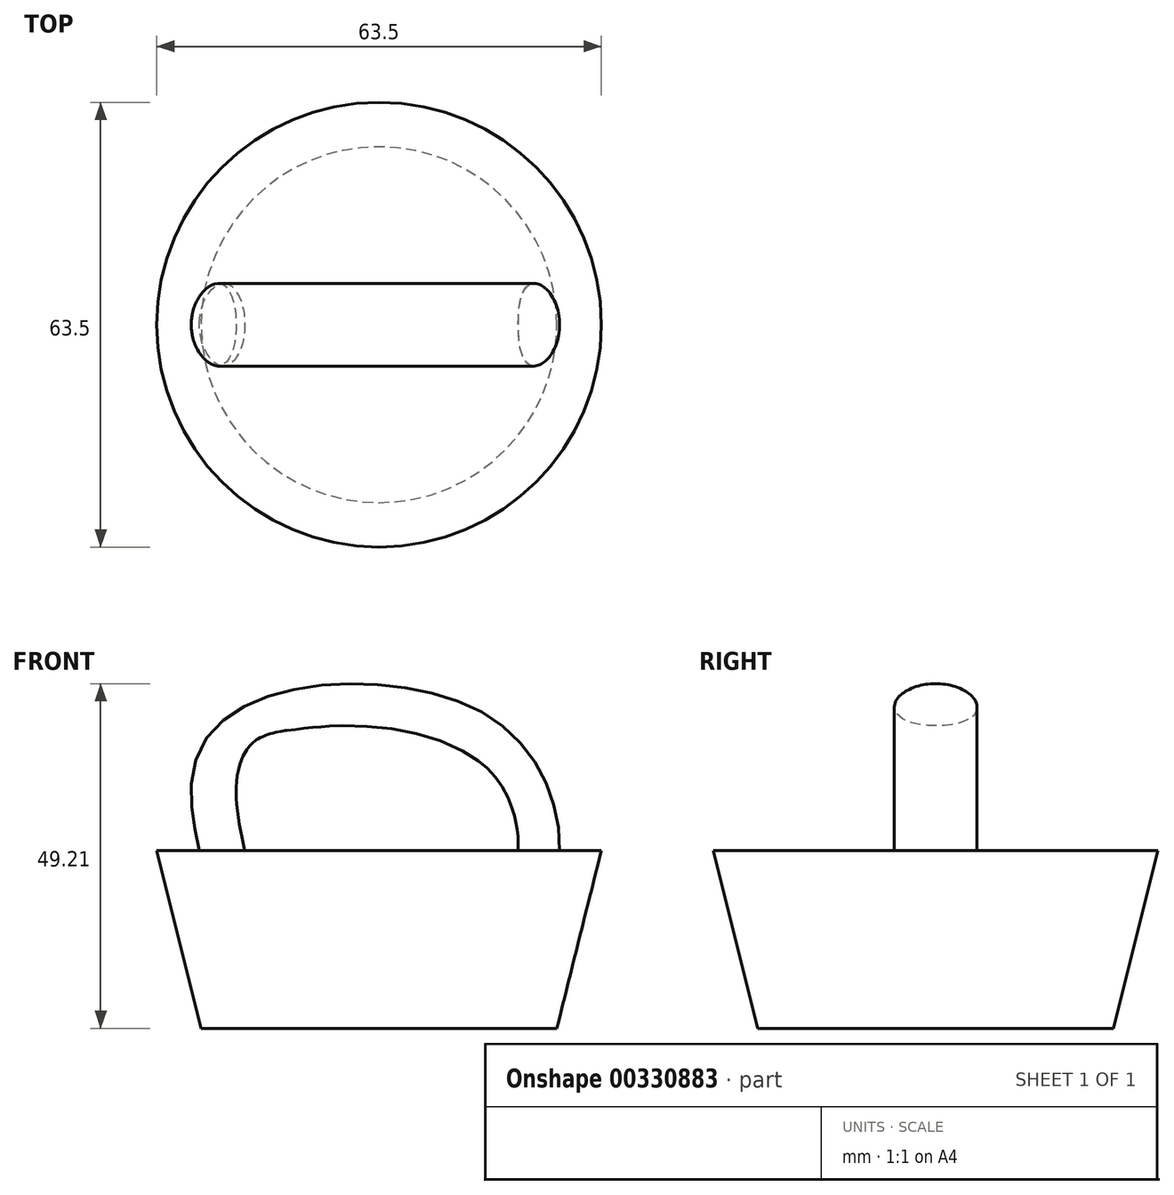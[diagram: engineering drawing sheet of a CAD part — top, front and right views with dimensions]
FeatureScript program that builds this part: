
annotation { "Feature Type Name" : "Feature", "Feature Type Description" : "" }
export const myFeature = defineFeature(function(context is Context, id is Id, definition is map)
    precondition{}
    {
        {
            var Q0;
            Q0=qCreatedBy(makeId("Top.planeOp"),FACE);
            var sketch = newSketch(context, id + "F0", { "sketchPlane" : qUnion([Q0])});
            skCircle(sketch, "E0", {"center": v(0, 0) * mm, "radius": 25.4 * mm});
            skSolve(sketch);
        }
        {
            var Q0;
            Q0=makeQuery(id+"F0.imprint","IMPRINT",FACE,{"disambiguationData":[TD([[makeQuery(id+"F0.imprint","IMPRINT",EDGE,{"derivedFrom":sQuery(id+"F0.wireOp",EDGE,"E0")}),1.0]])]});
            cPlane(context, id + "F1", {"entities" : qUnion([Q0]), "cplaneType" : CPlaneType.OFFSET, "offset" : 25.4 * mm, "width" : 152.4 * mm, "height" : 152.4 * mm});
        }
        {
            var Q0;
            Q0=qCreatedBy(id+"F1.planeOp",FACE);
            var sketch = newSketch(context, id + "F2", { "sketchPlane" : qUnion([Q0])});
            skCircle(sketch, "E1", {"center": v(0, 0) * mm, "radius": 31.75 * mm});
            skSolve(sketch);
        }
        {
            var Q0;
            Q0=makeQuery(id+"F2.imprint","IMPRINT",FACE,{"disambiguationData":[TD([[makeQuery(id+"F2.imprint","IMPRINT",EDGE,{"derivedFrom":sQuery(id+"F2.wireOp",EDGE,"E1")}),1.0]])]});
            var Q1;
            Q1=makeQuery(id+"F0.imprint","IMPRINT",FACE,{"disambiguationData":[TD([[makeQuery(id+"F0.imprint","IMPRINT",EDGE,{"derivedFrom":sQuery(id+"F0.wireOp",EDGE,"E0")}),1.0]])]});
            loft(context, id + "F3", {"sheetProfilesArray" : [{ "sheetProfileEntities" : qUnion([Q0]) }, { "sheetProfileEntities" : qUnion([Q1]) }]});
        }
        {
            var Q0;
            Q0=qCreatedBy(makeId("Front.planeOp"),FACE);
            var sketch = newSketch(context, id + "F4", { "sketchPlane" : qUnion([Q0])});
            skFitSpline(sketch, "E2", {"points": [v(0, 0) * mm, v(20.9, 18.84) * mm, v(14.13, 41.2) * mm, v(-19.72, 41.2) * mm, v(-20.3, 17.66) * mm], "startDerivative": vector(104.4, 63) * mm, "endDerivative": vector(31.4, -118.64) * mm});
            skSolve(sketch);
        }
        {
            var Q0;
            Q0=qCreatedBy(makeId("Top.planeOp"),FACE);
            var sketch = newSketch(context, id + "F5", { "sketchPlane" : qUnion([Q0])});
            skCircle(sketch, "E3", {"center": v(0, 0) * mm, "radius": 5.9 * mm});
            skSolve(sketch);
        }
        {
            var Q0;
            Q0=makeQuery(id+"F5.imprint","IMPRINT",FACE,{"disambiguationData":[TD([[makeQuery(id+"F5.imprint","IMPRINT",EDGE,{"derivedFrom":sQuery(id+"F5.wireOp",EDGE,"E3")}),1.0]])]});
            var Q1;
            Q1=sQuery(id+"F4.wireOp",EDGE,"E2");
            sweep(context, id + "F6", {"operationType" : NewBodyOperationType.ADD, "profiles" : qUnion([Q0]), "path" : qUnion([Q1])});
        }
    });
